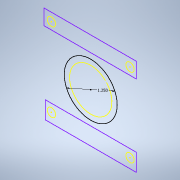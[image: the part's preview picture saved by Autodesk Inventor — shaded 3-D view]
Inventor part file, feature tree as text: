
AUTODESK INVENTOR PART (.ipt)
format: ipt  version: 2020 (Build 240168000, 168)  size: 118,784 bytes
history: native  units: in
note: dims shown in document units (in); Inventor stores cm internally (conversion verified against a paired STEP export)
features: reference x6, other x4, sketch x1, plane x1, extrude x1
ambient origin geometry x8: Origin, YZ Plane, XZ Plane, XY Plane, X Axis, Y Axis, Z Axis, Center Point
bodies: Solid1 (feature_tree)
feature tree (13):
  sketch  "Sketch1"  dims[d0=1.25in d1=0.25in d2=0.25in d3=2.375in d4=0.25in d5=1.0in d6=0.0in]
  plane  "Work Plane1"
  extrude  "Extrusion1"  Depth=2.375in
  reference  "Reference1"
  reference  "Reference2"
  reference  "Reference3"
  reference  "Reference4"
  reference  "Reference5"
  reference  "Reference6"
  other  "<userpath>\Desktop\PnP Machine\PnP Machine.iam"
  other  "PnP Machine.iam"
  other  "ST5918L4508-A:1"
  other  "9845T201_VIBRATE-DAMPING PRECISION FLEXIBLE SHAFT CPLG:1"
